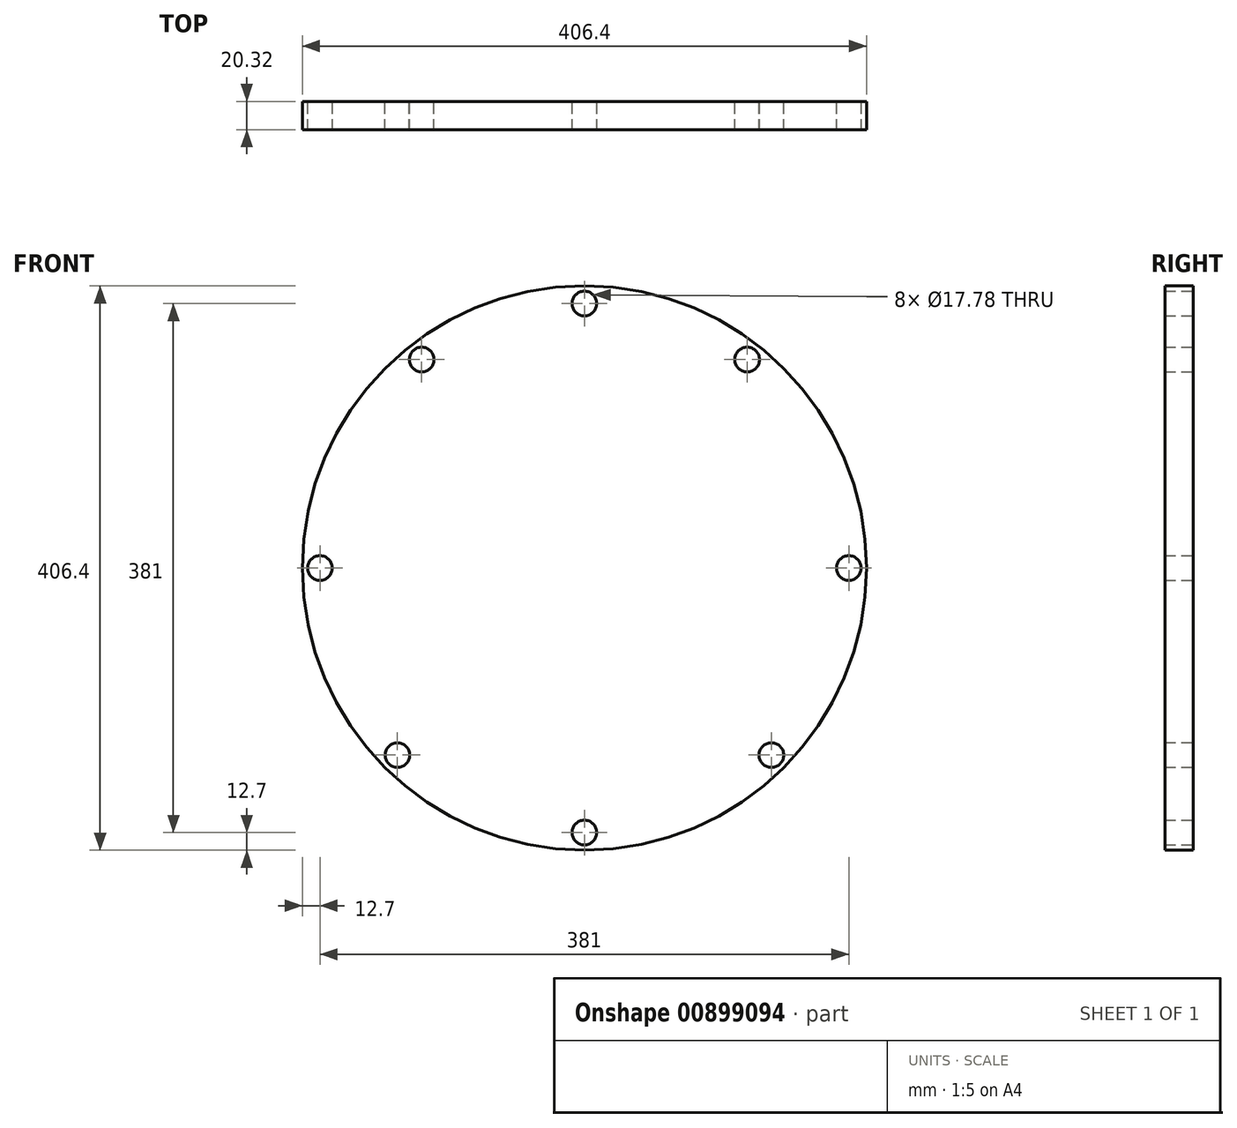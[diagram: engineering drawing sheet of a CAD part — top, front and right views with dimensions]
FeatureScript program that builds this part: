
annotation { "Feature Type Name" : "Feature", "Feature Type Description" : "" }
export const myFeature = defineFeature(function(context is Context, id is Id, definition is map)
    precondition{}
    {
        {
            var Q0;
            Q0=qCreatedBy(makeId("Front.planeOp"),FACE);
            var sketch = newSketch(context, id + "F0", { "sketchPlane" : qUnion([Q0])});
            skCircle(sketch, "E0", {"center": v(0, 0) * mm, "radius": 203.2 * mm});
            skCircle(sketch, "E1", {"center": v(0, 0) * mm, "radius": 190.5 * mm, "construction": true});
            skLineSegment(sketch, "E2", {"start": v(0, 0) * mm, "end": v(0, 190.5) * mm, "construction": true});
            skCircle(sketch, "E3", {"center": v(0, 190.5) * mm, "radius": 8.9 * mm});
            skCircle(sketch, "E4.2.0", {"center": v(-190.5, 0) * mm, "radius": 8.9 * mm});
            skCircle(sketch, "E4.3.0", {"center": v(-134.7, -134.7) * mm, "radius": 8.9 * mm});
            skCircle(sketch, "E4.4.0", {"center": v(0, -190.5) * mm, "radius": 8.9 * mm});
            skCircle(sketch, "E4.5.0", {"center": v(134.7, -134.7) * mm, "radius": 8.9 * mm});
            skCircle(sketch, "E4.6.0", {"center": v(190.5, 0) * mm, "radius": 8.9 * mm});
            skLineSegment(sketch, "E5", {"start": v(-134.7, 134.7) * mm, "end": v(-117.24, 150.15) * mm});
            skCircle(sketch, "E6", {"center": v(-117.24, 150.15) * mm, "radius": 8.9 * mm});
            skCircle(sketch, "E7.MirrorC", {"center": v(117.24, 150.15) * mm, "radius": 8.9 * mm});
            skSolve(sketch);
        }
        {
            var Q0;
            Q0 = qSketchRegion(id + "F0", true);
            extrude(context, id + "F1", {"entities" : qUnion([Q0]), "depth" : 20.32 * mm, "offsetDistance" : 25.4 * mm});
        }
    });
